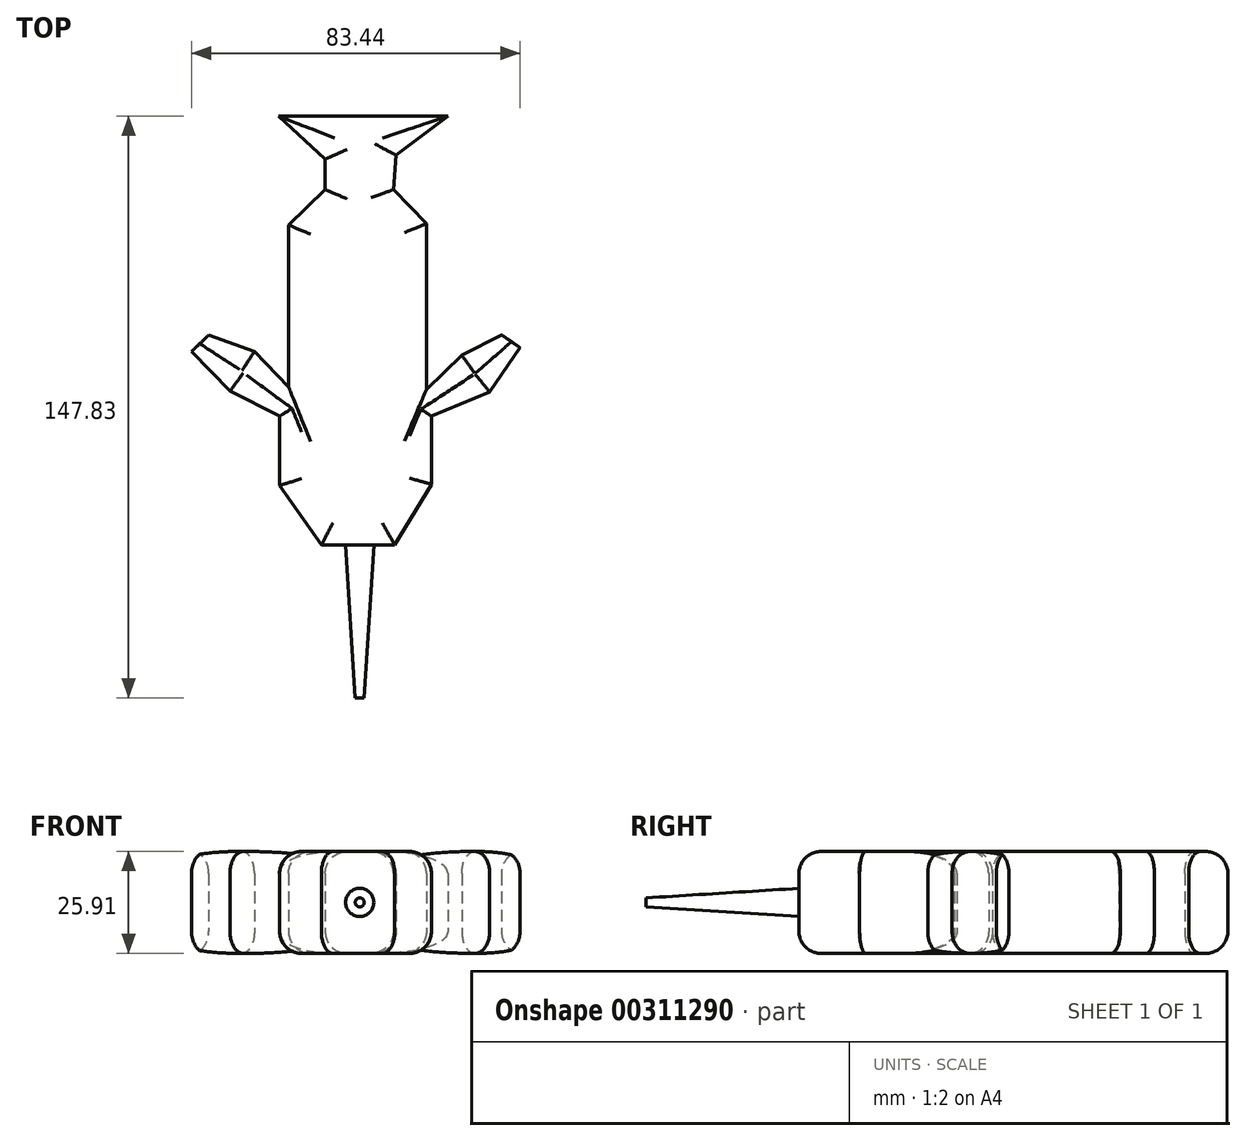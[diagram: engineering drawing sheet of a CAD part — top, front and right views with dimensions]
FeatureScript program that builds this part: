
annotation { "Feature Type Name" : "Feature", "Feature Type Description" : "" }
export const myFeature = defineFeature(function(context is Context, id is Id, definition is map)
    precondition{}
    {
        {
            var Q0;
            Q0=qCreatedBy(makeId("Top.planeOp"),FACE);
            var sketch = newSketch(context, id + "F0", { "sketchPlane" : qUnion([Q0])});
            skLineSegment(sketch, "E0", {"start": v(-20.36, 0) * mm, "end": v(-20.36, -17.61) * mm});
            skLineSegment(sketch, "E1", {"start": v(-20.36, -17.61) * mm, "end": v(-9.75, -32.72) * mm});
            skLineSegment(sketch, "E2", {"start": v(-9.75, -32.72) * mm, "end": v(0, -32.72) * mm});
            skLineSegment(sketch, "E3", {"start": v(0, -32.72) * mm, "end": v(8.9, -32.72) * mm});
            skLineSegment(sketch, "E4", {"start": v(8.9, -32.72) * mm, "end": v(18.21, -17.3) * mm});
            skLineSegment(sketch, "E5", {"start": v(18.21, -17.3) * mm, "end": v(18.21, 0) * mm});
            skLineSegment(sketch, "E6", {"start": v(18.21, 0) * mm, "end": v(33, 6.17) * mm});
            skLineSegment(sketch, "E7", {"start": v(33, 6.17) * mm, "end": v(40.71, 17.42) * mm});
            skLineSegment(sketch, "E8", {"start": v(40.71, 17.42) * mm, "end": v(36, 20.65) * mm});
            skLineSegment(sketch, "E9", {"start": v(36, 20.65) * mm, "end": v(25.93, 15.5) * mm});
            skLineSegment(sketch, "E10", {"start": v(25.93, 15.5) * mm, "end": v(16.93, 6.82) * mm});
            skLineSegment(sketch, "E11", {"start": v(16.93, 6.82) * mm, "end": v(16.93, 30.6) * mm});
            skLineSegment(sketch, "E12", {"start": v(16.93, 30.6) * mm, "end": v(16.93, 48.93) * mm});
            skLineSegment(sketch, "E13", {"start": v(16.93, 48.93) * mm, "end": v(8.57, 57.6) * mm});
            skLineSegment(sketch, "E14", {"start": v(8.57, 57.6) * mm, "end": v(0, 57.6) * mm});
            skLineSegment(sketch, "E15", {"start": v(0, 57.6) * mm, "end": v(-8.79, 57.6) * mm});
            skLineSegment(sketch, "E16", {"start": v(-8.79, 57.6) * mm, "end": v(-18.1, 48.61) * mm});
            skLineSegment(sketch, "E17", {"start": v(-18.1, 48.61) * mm, "end": v(-18.1, 28.68) * mm});
            skLineSegment(sketch, "E18", {"start": v(-18.1, 28.68) * mm, "end": v(-18.1, 7.46) * mm});
            skLineSegment(sketch, "E19", {"start": v(-18.1, 7.46) * mm, "end": v(-26.76, 16.44) * mm});
            skLineSegment(sketch, "E20", {"start": v(-26.76, 16.44) * mm, "end": v(-38.36, 20.65) * mm});
            skLineSegment(sketch, "E21", {"start": v(-38.36, 20.65) * mm, "end": v(-42.73, 16.44) * mm});
            skLineSegment(sketch, "E22", {"start": v(-42.73, 16.44) * mm, "end": v(-33, 6.34) * mm});
            skLineSegment(sketch, "E23", {"start": v(-33, 6.34) * mm, "end": v(-20.36, 0) * mm});
            skLineSegment(sketch, "E24", {"start": v(-8.79, 57.6) * mm, "end": v(-8.79, 65.32) * mm});
            skLineSegment(sketch, "E25", {"start": v(-8.79, 65.32) * mm, "end": v(-20.68, 76.25) * mm});
            skLineSegment(sketch, "E26", {"start": v(-20.68, 76.25) * mm, "end": v(22.4, 76.25) * mm});
            skLineSegment(sketch, "E27", {"start": v(22.4, 76.25) * mm, "end": v(9.21, 66.29) * mm});
            skLineSegment(sketch, "E28", {"start": v(9.21, 66.29) * mm, "end": v(8.57, 57.6) * mm});
            skSolve(sketch);
        }
        {
            var Q0;
            Q0=makeQuery(id+"F0.imprint","IMPRINT",FACE,{"disambiguationData":[TD([[makeQuery(id+"F0.imprint","IMPRINT",EDGE,{"derivedFrom":sQuery(id+"F0.wireOp",EDGE,"E0")}),1.0]])]});
            var Q1;
            Q1=makeQuery(id+"F0.imprint","IMPRINT",FACE,{"disambiguationData":[TD([[makeQuery(id+"F0.imprint","IMPRINT",EDGE,{"derivedFrom":sQuery(id+"F0.wireOp",EDGE,"E14")}),-1.0]])]});
            extrude(context, id + "F1", {"entities" : qUnion([Q0, Q1]), "depth" : 25.9 * mm});
        }
        {
            var Q0;
            Q0=makeQuery(id+"F1.opExtrude","CAP_FACE",FACE,{"disambiguationData":[OSD([sQuery(id+"F0.wireOp",EDGE,"E0"),sQuery(id+"F0.wireOp",EDGE,"E1"),sQuery(id+"F0.wireOp",EDGE,"E2"),sQuery(id+"F0.wireOp",EDGE,"E3"),sQuery(id+"F0.wireOp",EDGE,"E4"),sQuery(id+"F0.wireOp",EDGE,"E5"),sQuery(id+"F0.wireOp",EDGE,"E6"),sQuery(id+"F0.wireOp",EDGE,"E7"),sQuery(id+"F0.wireOp",EDGE,"E8"),sQuery(id+"F0.wireOp",EDGE,"E9"),sQuery(id+"F0.wireOp",EDGE,"E10"),sQuery(id+"F0.wireOp",EDGE,"E11"),sQuery(id+"F0.wireOp",EDGE,"E12"),sQuery(id+"F0.wireOp",EDGE,"E13"),sQuery(id+"F0.wireOp",EDGE,"E16"),sQuery(id+"F0.wireOp",EDGE,"E17"),sQuery(id+"F0.wireOp",EDGE,"E18"),sQuery(id+"F0.wireOp",EDGE,"E19"),sQuery(id+"F0.wireOp",EDGE,"E20"),sQuery(id+"F0.wireOp",EDGE,"E21"),sQuery(id+"F0.wireOp",EDGE,"E22"),sQuery(id+"F0.wireOp",EDGE,"E23"),sQuery(id+"F0.wireOp",EDGE,"E24"),sQuery(id+"F0.wireOp",EDGE,"E25"),sQuery(id+"F0.wireOp",EDGE,"E26"),sQuery(id+"F0.wireOp",EDGE,"E27"),sQuery(id+"F0.wireOp",EDGE,"E28")])],"isStart":false});
            var Q1;
            Q1=makeQuery(id+"F1.opExtrude","CAP_FACE",FACE,{"disambiguationData":[OSD([sQuery(id+"F0.wireOp",EDGE,"E0"),sQuery(id+"F0.wireOp",EDGE,"E1"),sQuery(id+"F0.wireOp",EDGE,"E2"),sQuery(id+"F0.wireOp",EDGE,"E3"),sQuery(id+"F0.wireOp",EDGE,"E4"),sQuery(id+"F0.wireOp",EDGE,"E5"),sQuery(id+"F0.wireOp",EDGE,"E6"),sQuery(id+"F0.wireOp",EDGE,"E7"),sQuery(id+"F0.wireOp",EDGE,"E8"),sQuery(id+"F0.wireOp",EDGE,"E9"),sQuery(id+"F0.wireOp",EDGE,"E10"),sQuery(id+"F0.wireOp",EDGE,"E11"),sQuery(id+"F0.wireOp",EDGE,"E12"),sQuery(id+"F0.wireOp",EDGE,"E13"),sQuery(id+"F0.wireOp",EDGE,"E16"),sQuery(id+"F0.wireOp",EDGE,"E17"),sQuery(id+"F0.wireOp",EDGE,"E18"),sQuery(id+"F0.wireOp",EDGE,"E19"),sQuery(id+"F0.wireOp",EDGE,"E20"),sQuery(id+"F0.wireOp",EDGE,"E21"),sQuery(id+"F0.wireOp",EDGE,"E22"),sQuery(id+"F0.wireOp",EDGE,"E23"),sQuery(id+"F0.wireOp",EDGE,"E24"),sQuery(id+"F0.wireOp",EDGE,"E25"),sQuery(id+"F0.wireOp",EDGE,"E26"),sQuery(id+"F0.wireOp",EDGE,"E27"),sQuery(id+"F0.wireOp",EDGE,"E28")])],"isStart":true});
            fillet(context, id + "F2", {"entities" : qUnion([Q0, Q1]), "radius" : 5.6 * mm, "tangentPropagation" : true, "allowEdgeOverflow" : false});
        }
        {
            var Q0;
            Q0=makeQuery(id+"F1.opExtrude","SWEPT_FACE",FACE,{"disambiguationData":[OSD([sQuery(id+"F0.wireOp",EDGE,"E2"),sQuery(id+"F0.wireOp",EDGE,"E3")])]});
            var sketch = newSketch(context, id + "F3", { "sketchPlane" : qUnion([Q0])});
            skCircle(sketch, "E29", {"center": v(0, 12.95) * mm, "radius": 3.7 * mm});
            skSolve(sketch);
        }
        {
            var Q0;
            Q0=makeQuery(id+"F3.imprint","IMPRINT",FACE,{"disambiguationData":[TD([[makeQuery(id+"F3.imprint","IMPRINT",EDGE,{"derivedFrom":sQuery(id+"F3.wireOp",EDGE,"E29")}),1.0]])]});
            extrude(context, id + "F4", {"entities" : qUnion([Q0]), "operationType" : NewBodyOperationType.ADD, "depth" : 38.86 * mm});
        }
        {
            var Q0;
            Q0=makeQuery(id+"F4.opExtrude","CAP_EDGE",EDGE,{"disambiguationData":[OSD([sQuery(id+"F3.wireOp",EDGE,"E29")])],"isStart":false});
            chamfer(context, id + "F5", {"entities" : qUnion([Q0]), "chamferType" : ChamferType.TWO_OFFSETS, "width1" : 2.54 * mm, "oppositeDirection" : false, "width2" : 40.64 * mm, "tangentPropagation" : true});
        }
    });
